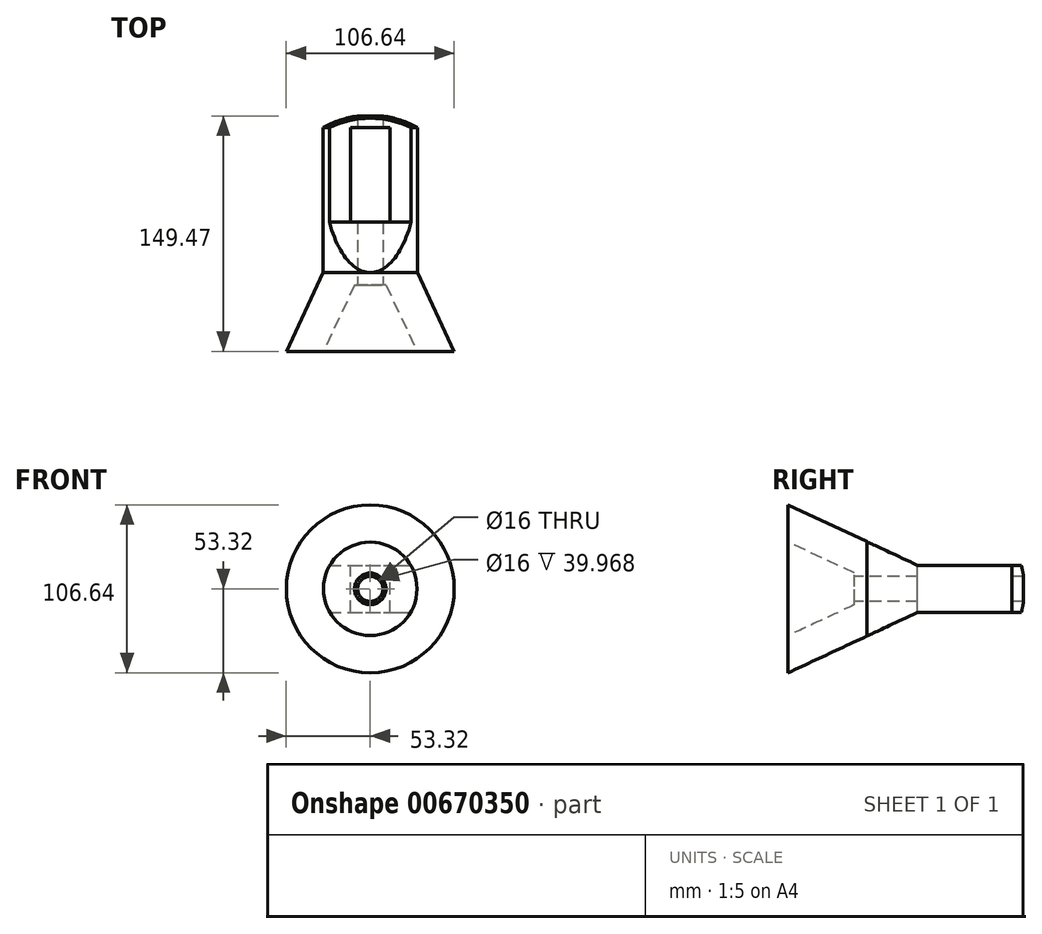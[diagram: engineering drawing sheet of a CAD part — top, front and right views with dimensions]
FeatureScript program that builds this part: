
annotation { "Feature Type Name" : "Feature", "Feature Type Description" : "" }
export const myFeature = defineFeature(function(context is Context, id is Id, definition is map)
    precondition{}
    {
        {
            var Q0;
            Q0=qCreatedBy(makeId("Top.planeOp"),FACE);
            var sketch = newSketch(context, id + "F0", { "sketchPlane" : qUnion([Q0])});
            skLineSegment(sketch, "E0", {"start": v(0, 0) * mm, "end": v(0, 89.63) * mm});
            skLineSegment(sketch, "E1", {"start": v(-53.32, 0) * mm, "end": v(-30, 50) * mm});
            skLineSegment(sketch, "E2", {"start": v(-30, 50) * mm, "end": v(-30, 142.11) * mm});
            skLineSegment(sketch, "E3", {"start": v(-53.32, 0) * mm, "end": v(-29.68, 0) * mm});
            skLineSegment(sketch, "E4", {"start": v(-29.68, 0) * mm, "end": v(-10, 42.2) * mm});
            skLineSegment(sketch, "E5", {"start": v(-10, 42.2) * mm, "end": v(-8, 42.2) * mm});
            skLineSegment(sketch, "E6", {"start": v(-8, 42.2) * mm, "end": v(-8, 150) * mm});
            skArc(sketch, "E7", {"start": v(-8, 149.47) * mm, "mid": v(-19.35, 146.85) * mm, "end": v(-30, 142.11) * mm});
            skPoint(sketch, "E8.start.orphan", {"position": v(-30, 150) * mm});
            skSolve(sketch);
        }
        {
            var Q0;
            Q0 = qSketchRegion(id + "F0", true);
            var Q1;
            Q1=sQuery(id+"F0.wireOp",EDGE,"E0");
            revolve(context, id + "F1", {"entities" : qUnion([Q0]), "axis" : qUnion([Q1]), "revolveType" : RevolveType.FULL});
        }
        {
            var Q0;
            Q0=qCreatedBy(makeId("Right.planeOp"),FACE);
            var sketch = newSketch(context, id + "F2", { "sketchPlane" : qUnion([Q0])});
            skLineSegment(sketch, "E9", {"start": v(50, 30) * mm, "end": v(82.17, 15) * mm});
            skLineSegment(sketch, "E10", {"start": v(82.17, 15) * mm, "end": v(149.47, 15) * mm});
            skLineSegment(sketch, "E11", {"start": v(149.47, 15) * mm, "end": v(149.47, 30) * mm});
            skLineSegment(sketch, "E12", {"start": v(149.47, 30) * mm, "end": v(50, 30) * mm});
            skPoint(sketch, "E13", {"position": v(50, 30) * mm});
            skLineSegment(sketch, "E14", {"start": v(0, 0) * mm, "end": v(50, 0) * mm});
            skLineSegment(sketch, "E15", {"start": v(50, 0) * mm, "end": v(50, 30) * mm});
            skSolve(sketch);
        }
        {
            var Q0;
            Q0=makeQuery(id+"F2.imprint","IMPRINT",FACE,{"disambiguationData":[TD([[makeQuery(id+"F2.imprint","IMPRINT",EDGE,{"derivedFrom":sQuery(id+"F2.wireOp",EDGE,"E9")}),1.0]])]});
            extrude(context, id + "F3", {"entities" : qUnion([Q0]), "operationType" : NewBodyOperationType.REMOVE, "endBound" : BoundingType.SYMMETRIC, "oppositeDirection" : true, "depth" : 60 * mm, "offsetDistance" : 25 * mm});
        }
        {
            var Q0;
            Q0=makeQuery(id+"F1.opRevolve","SWEPT_BODY",BODY,{"disambiguationData":[OSD([sQuery(id+"F0.wireOp",EDGE,"E1"),sQuery(id+"F0.wireOp",EDGE,"E2"),sQuery(id+"F0.wireOp",EDGE,"E3"),sQuery(id+"F0.wireOp",EDGE,"E4"),sQuery(id+"F0.wireOp",EDGE,"E5"),sQuery(id+"F0.wireOp",EDGE,"E6"),sQuery(id+"F0.wireOp",EDGE,"E7")])]});
            var Q1;
            Q1=qCreatedBy(makeId("Top.planeOp"),FACE);
            mirror(context, id + "F4", {"operationType" : NewBodyOperationType.INTERSECT, "entities" : qUnion([Q0]), "mirrorPlane" : qUnion([Q1])});
        }
        {
            var Q0;
            Q0=makeQuery(id+"F3.boolean.opBoolean","COPY",FACE,{"derivedFrom":makeQuery(id+"F3.opExtrude","SWEPT_FACE",FACE,{"disambiguationData":[OSD([sQuery(id+"F2.wireOp",EDGE,"E10")])]})});
            var sketch = newSketch(context, id + "F5", { "sketchPlane" : qUnion([Q0])});
            skLineSegment(sketch, "E16.bottom", {"start": v(-12.5, 142.17) * mm, "end": v(12.5, 142.17) * mm});
            skLineSegment(sketch, "E16.top", {"start": v(-12.5, 82.17) * mm, "end": v(12.5, 82.17) * mm});
            skLineSegment(sketch, "E16.left", {"start": v(-12.5, 142.17) * mm, "end": v(-12.5, 82.17) * mm});
            skLineSegment(sketch, "E16.right", {"start": v(12.5, 142.17) * mm, "end": v(12.5, 82.17) * mm});
            skSolve(sketch);
        }
        {
            var Q0;
            Q0=makeQuery(id+"F5.imprint","IMPRINT",FACE,{"disambiguationData":[TD([[makeQuery(id+"F5.imprint","IMPRINT",EDGE,{"derivedFrom":sQuery(id+"F5.wireOp",EDGE,"E16.bottom")}),-1.0]])]});
            extrude(context, id + "F6", {"entities" : qUnion([Q0]), "operationType" : NewBodyOperationType.REMOVE, "endBound" : BoundingType.THROUGH_ALL, "oppositeDirection" : true, "depth" : 25 * mm, "offsetDistance" : 25 * mm});
        }
    });
